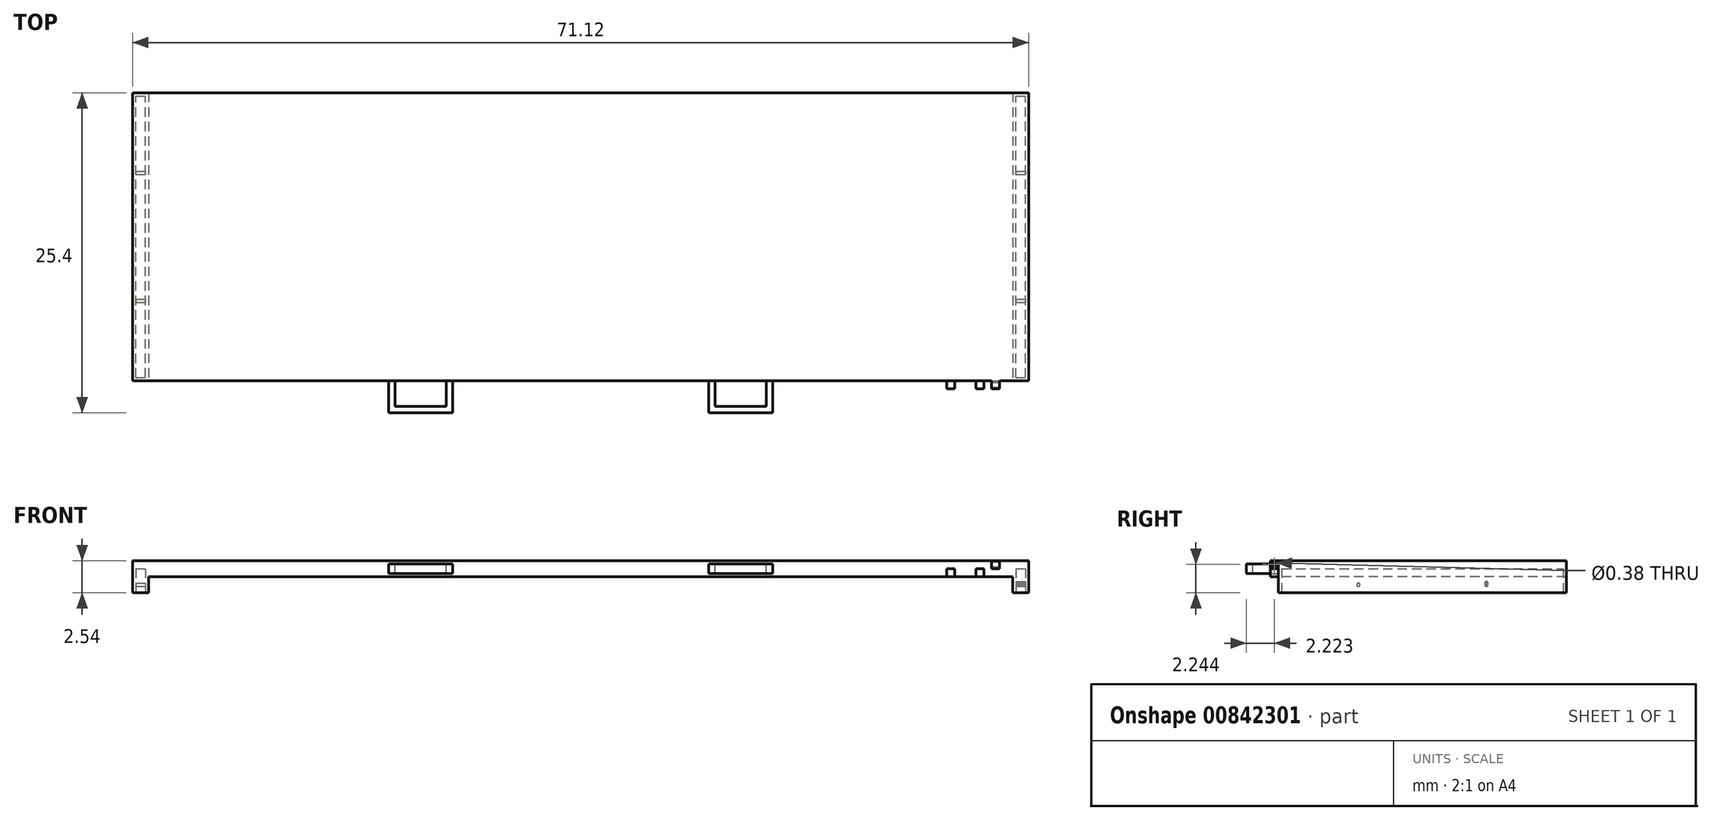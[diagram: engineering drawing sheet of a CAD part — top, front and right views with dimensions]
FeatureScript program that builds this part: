
annotation { "Feature Type Name" : "Feature", "Feature Type Description" : "" }
export const myFeature = defineFeature(function(context is Context, id is Id, definition is map)
    precondition{}
    {
        {
            var Q0;
            Q0=qCreatedBy(makeId("Front.planeOp"),FACE);
            var sketch = newSketch(context, id + "F0", { "sketchPlane" : qUnion([Q0])});
            skLineSegment(sketch, "E0.bottom", {"start": v(-23.07, 23.36) * mm, "end": v(48.05, 23.36) * mm});
            skLineSegment(sketch, "E0.top", {"start": v(-23.07, 20.82) * mm, "end": v(48.05, 20.82) * mm});
            skLineSegment(sketch, "E0.left", {"start": v(-23.07, 23.36) * mm, "end": v(-23.07, 20.82) * mm});
            skLineSegment(sketch, "E0.right", {"start": v(48.05, 23.36) * mm, "end": v(48.05, 20.82) * mm});
            skSolve(sketch);
        }
        {
            var Q0;
            Q0 = qSketchRegion(id + "F0", true);
            extrude(context, id + "F1", {"entities" : qUnion([Q0]), "depth" : 22.86 * mm, "offsetDistance" : 25.4 * mm});
        }
        {
            var Q0;
            Q0=makeQuery(id+"F1.opExtrude","CAP_FACE",FACE,{"disambiguationData":[OSD([sQuery(id+"F0.wireOp",EDGE,"E0.bottom"),sQuery(id+"F0.wireOp",EDGE,"E0.top"),sQuery(id+"F0.wireOp",EDGE,"E0.left"),sQuery(id+"F0.wireOp",EDGE,"E0.right")])],"isStart":false});
            var sketch = newSketch(context, id + "F2", { "sketchPlane" : qUnion([Q0])});
            skLineSegment(sketch, "E1.bottom", {"start": v(-21.8, 20.82) * mm, "end": v(46.78, 20.82) * mm});
            skLineSegment(sketch, "E1.top", {"start": v(-21.8, 22.1) * mm, "end": v(46.78, 22.1) * mm});
            skLineSegment(sketch, "E1.left", {"start": v(-21.8, 20.82) * mm, "end": v(-21.8, 22.1) * mm});
            skLineSegment(sketch, "E1.right", {"start": v(46.78, 20.82) * mm, "end": v(46.78, 22.1) * mm});
            skSolve(sketch);
        }
        {
            var Q0;
            Q0 = qSketchRegion(id + "F2", true);
            extrude(context, id + "F3", {"entities" : qUnion([Q0]), "operationType" : NewBodyOperationType.REMOVE, "oppositeDirection" : true, "depth" : 22.86 * mm, "offsetDistance" : 25.4 * mm});
        }
        {
            var Q0;
            {var subQ0=sQuery(id+"F0.wireOp",EDGE,"E0.right");var subQ2=sQuery(id+"F0.wireOp",EDGE,"E0.top");Q0=makeQuery(id+"F3.boolean.opBoolean","SPLIT",FACE,{"disambiguationData":[TD([makeQuery(id+"F1.opExtrude","SWEPT_FACE",FACE,{"disambiguationData":[OSD([subQ0])]})])],"derivedFrom":makeQuery(id+"F1.opExtrude","SWEPT_FACE",FACE,{"disambiguationData":[OSD([subQ2])]})});}
            var sketch = newSketch(context, id + "F4", { "sketchPlane" : qUnion([Q0])});
            skLineSegment(sketch, "E2.bottom", {"start": v(47.03, 22.6) * mm, "end": v(47.8, 22.6) * mm});
            skLineSegment(sketch, "E2.top", {"start": v(47.03, 0.25) * mm, "end": v(47.8, 0.25) * mm});
            skLineSegment(sketch, "E2.left", {"start": v(47.03, 22.6) * mm, "end": v(47.03, 0.25) * mm});
            skLineSegment(sketch, "E2.right", {"start": v(47.8, 22.6) * mm, "end": v(47.8, 0.25) * mm});
            skSolve(sketch);
        }
        {
            var Q0;
            Q0 = qSketchRegion(id + "F4", true);
            extrude(context, id + "F5", {"entities" : qUnion([Q0]), "operationType" : NewBodyOperationType.REMOVE, "oppositeDirection" : true, "depth" : 1.9 * mm, "offsetDistance" : 25.4 * mm});
        }
        {
            var Q0;
            {var subQ1=sQuery(id+"F0.wireOp",EDGE,"E0.left");var subQ2=sQuery(id+"F0.wireOp",EDGE,"E0.top");Q0=makeQuery(id+"F3.boolean.opBoolean","SPLIT",FACE,{"disambiguationData":[TD([makeQuery(id+"F1.opExtrude","SWEPT_FACE",FACE,{"disambiguationData":[OSD([subQ1])]})])],"derivedFrom":makeQuery(id+"F1.opExtrude","SWEPT_FACE",FACE,{"disambiguationData":[OSD([subQ2])]})});}
            var sketch = newSketch(context, id + "F6", { "sketchPlane" : qUnion([Q0])});
            skLineSegment(sketch, "E3.bottom", {"start": v(-22.82, 22.6) * mm, "end": v(-22.05, 22.6) * mm});
            skLineSegment(sketch, "E3.top", {"start": v(-22.82, 0.25) * mm, "end": v(-22.05, 0.25) * mm});
            skLineSegment(sketch, "E3.left", {"start": v(-22.82, 22.6) * mm, "end": v(-22.82, 0.25) * mm});
            skLineSegment(sketch, "E3.right", {"start": v(-22.05, 22.6) * mm, "end": v(-22.05, 0.25) * mm});
            skSolve(sketch);
        }
        {
            var Q0;
            Q0 = qSketchRegion(id + "F6", true);
            extrude(context, id + "F7", {"entities" : qUnion([Q0]), "operationType" : NewBodyOperationType.REMOVE, "oppositeDirection" : true, "depth" : 1.9 * mm, "offsetDistance" : 25.4 * mm});
        }
        {
            var Q0;
            Q0=makeQuery(id+"F5.boolean.opBoolean","COPY",FACE,{"derivedFrom":makeQuery(id+"F5.opExtrude","SWEPT_FACE",FACE,{"disambiguationData":[OSD([sQuery(id+"F4.wireOp",EDGE,"E2.right")])]})});
            var sketch = newSketch(context, id + "F8", { "sketchPlane" : qUnion([Q0])});
            skCircle(sketch, "E4", {"center": v(16.5, 21.46) * mm, "radius": 0.13 * mm});
            skCircle(sketch, "E5", {"center": v(6.35, 21.59) * mm, "radius": 0.13 * mm});
            skSolve(sketch);
        }
        {
            var Q0;
            Q0 = qSketchRegion(id + "F8", true);
            extrude(context, id + "F9", {"entities" : qUnion([Q0]), "operationType" : NewBodyOperationType.ADD, "endBound" : BoundingType.UP_TO_NEXT, "depth" : 25.4 * mm, "offsetDistance" : 25.4 * mm});
        }
        {
            var Q0;
            Q0=makeQuery(id+"F7.boolean.opBoolean","COPY",FACE,{"derivedFrom":makeQuery(id+"F7.opExtrude","SWEPT_FACE",FACE,{"disambiguationData":[OSD([sQuery(id+"F6.wireOp",EDGE,"E3.right")])]})});
            var sketch = newSketch(context, id + "F10", { "sketchPlane" : qUnion([Q0])});
            skCircle(sketch, "E6", {"center": v(16.51, 21.46) * mm, "radius": 0.13 * mm});
            skCircle(sketch, "E7", {"center": v(6.35, 21.46) * mm, "radius": 0.13 * mm});
            skSolve(sketch);
        }
        {
            var Q0;
            Q0 = qSketchRegion(id + "F10", true);
            extrude(context, id + "F11", {"entities" : qUnion([Q0]), "operationType" : NewBodyOperationType.ADD, "endBound" : BoundingType.UP_TO_NEXT, "depth" : 25.4 * mm, "offsetDistance" : 25.4 * mm});
        }
        {
            var Q0;
            Q0=makeQuery(id+"F1.opExtrude","CAP_FACE",FACE,{"disambiguationData":[OSD([sQuery(id+"F0.wireOp",EDGE,"E0.bottom"),sQuery(id+"F0.wireOp",EDGE,"E0.top"),sQuery(id+"F0.wireOp",EDGE,"E0.left"),sQuery(id+"F0.wireOp",EDGE,"E0.right")])],"isStart":false});
            var sketch = newSketch(context, id + "F12", { "sketchPlane" : qUnion([Q0])});
            skLineSegment(sketch, "E8.bottom", {"start": v(-2.75, 23.11) * mm, "end": v(2.33, 23.11) * mm});
            skLineSegment(sketch, "E8.top", {"start": v(-2.75, 22.35) * mm, "end": v(2.33, 22.35) * mm});
            skLineSegment(sketch, "E8.left", {"start": v(-2.75, 23.11) * mm, "end": v(-2.75, 22.35) * mm});
            skLineSegment(sketch, "E8.right", {"start": v(2.33, 23.11) * mm, "end": v(2.33, 22.35) * mm});
            skLineSegment(sketch, "E9.bottom", {"start": v(22.65, 23.11) * mm, "end": v(27.73, 23.11) * mm});
            skLineSegment(sketch, "E9.top", {"start": v(22.65, 22.35) * mm, "end": v(27.73, 22.35) * mm});
            skLineSegment(sketch, "E9.left", {"start": v(22.65, 23.11) * mm, "end": v(22.65, 22.35) * mm});
            skLineSegment(sketch, "E9.right", {"start": v(27.73, 23.11) * mm, "end": v(27.73, 22.35) * mm});
            skSolve(sketch);
        }
        {
            var Q0;
            Q0 = qSketchRegion(id + "F12", true);
            extrude(context, id + "F13", {"entities" : qUnion([Q0]), "operationType" : NewBodyOperationType.ADD, "depth" : 2.54 * mm, "offsetDistance" : 25.4 * mm});
        }
        {
            var Q0;
            Q0=makeQuery(id+"F13.opExtrude","SWEPT_FACE",FACE,{"disambiguationData":[OSD([sQuery(id+"F12.wireOp",EDGE,"E9.bottom")])]});
            var sketch = newSketch(context, id + "F14", { "sketchPlane" : qUnion([Q0])});
            skLineSegment(sketch, "E10.bottom", {"start": v(23.16, -22.86) * mm, "end": v(27.22, -22.86) * mm});
            skLineSegment(sketch, "E10.top", {"start": v(23.16, -24.9) * mm, "end": v(27.22, -24.9) * mm});
            skLineSegment(sketch, "E10.left", {"start": v(23.16, -22.86) * mm, "end": v(23.16, -24.9) * mm});
            skLineSegment(sketch, "E10.right", {"start": v(27.22, -22.86) * mm, "end": v(27.22, -24.9) * mm});
            skSolve(sketch);
        }
        {
            var Q0;
            Q0 = qSketchRegion(id + "F14", true);
            extrude(context, id + "F15", {"entities" : qUnion([Q0]), "operationType" : NewBodyOperationType.REMOVE, "endBound" : BoundingType.THROUGH_ALL, "oppositeDirection" : true, "depth" : 25.4 * mm, "offsetDistance" : 25.4 * mm});
        }
        {
            var Q0;
            Q0=makeQuery(id+"F13.opExtrude","SWEPT_FACE",FACE,{"disambiguationData":[OSD([sQuery(id+"F12.wireOp",EDGE,"E8.bottom")])]});
            var sketch = newSketch(context, id + "F16", { "sketchPlane" : qUnion([Q0])});
            skLineSegment(sketch, "E11.bottom", {"start": v(-2.24, -22.86) * mm, "end": v(1.82, -22.86) * mm});
            skLineSegment(sketch, "E11.top", {"start": v(-2.24, -24.9) * mm, "end": v(1.82, -24.9) * mm});
            skLineSegment(sketch, "E11.left", {"start": v(-2.24, -22.86) * mm, "end": v(-2.24, -24.9) * mm});
            skLineSegment(sketch, "E11.right", {"start": v(1.82, -22.86) * mm, "end": v(1.82, -24.9) * mm});
            skSolve(sketch);
        }
        {
            var Q0;
            Q0 = qSketchRegion(id + "F16", true);
            extrude(context, id + "F17", {"entities" : qUnion([Q0]), "operationType" : NewBodyOperationType.REMOVE, "endBound" : BoundingType.THROUGH_ALL, "oppositeDirection" : true, "depth" : 25.4 * mm, "offsetDistance" : 25.4 * mm});
        }
        {
            var Q0;
            Q0=makeQuery(id+"F17.boolean.opBoolean","MERGE",FACE,{"derivedFrom":[makeQuery(id+"F15.boolean.opBoolean","MERGE",FACE,{"derivedFrom":[makeQuery(id+"F1.opExtrude","CAP_FACE",FACE,{"disambiguationData":[OSD([sQuery(id+"F0.wireOp",EDGE,"E0.bottom"),sQuery(id+"F0.wireOp",EDGE,"E0.top"),sQuery(id+"F0.wireOp",EDGE,"E0.left"),sQuery(id+"F0.wireOp",EDGE,"E0.right")])],"isStart":false}),makeQuery(id+"F15.opExtrude","SWEPT_FACE",FACE,{"disambiguationData":[OSD([sQuery(id+"F14.wireOp",EDGE,"E10.bottom")])]})]}),makeQuery(id+"F17.opExtrude","SWEPT_FACE",FACE,{"disambiguationData":[OSD([sQuery(id+"F16.wireOp",EDGE,"E11.bottom")])]})]});
            var sketch = newSketch(context, id + "F18", { "sketchPlane" : qUnion([Q0])});
            skLineSegment(sketch, "E12.bottom", {"start": v(45.12, 23.36) * mm, "end": v(45.75, 23.36) * mm});
            skLineSegment(sketch, "E12.top", {"start": v(45.12, 22.73) * mm, "end": v(45.75, 22.73) * mm});
            skLineSegment(sketch, "E12.left", {"start": v(45.12, 23.36) * mm, "end": v(45.12, 22.73) * mm});
            skLineSegment(sketch, "E12.right", {"start": v(45.75, 23.36) * mm, "end": v(45.75, 22.73) * mm});
            skLineSegment(sketch, "E13.bottom", {"start": v(43.86, 22.1) * mm, "end": v(44.5, 22.1) * mm});
            skLineSegment(sketch, "E13.top", {"start": v(43.86, 22.73) * mm, "end": v(44.5, 22.73) * mm});
            skLineSegment(sketch, "E13.left", {"start": v(43.86, 22.1) * mm, "end": v(43.86, 22.73) * mm});
            skLineSegment(sketch, "E13.right", {"start": v(44.5, 22.1) * mm, "end": v(44.5, 22.73) * mm});
            skLineSegment(sketch, "E14.bottom", {"start": v(41.55, 22.1) * mm, "end": v(42.18, 22.1) * mm});
            skLineSegment(sketch, "E14.top", {"start": v(41.55, 22.73) * mm, "end": v(42.18, 22.73) * mm});
            skLineSegment(sketch, "E14.left", {"start": v(41.55, 22.1) * mm, "end": v(41.55, 22.73) * mm});
            skLineSegment(sketch, "E14.right", {"start": v(42.18, 22.1) * mm, "end": v(42.18, 22.73) * mm});
            skSolve(sketch);
        }
        {
            var Q0;
            Q0 = qSketchRegion(id + "F18", true);
            extrude(context, id + "F19", {"entities" : qUnion([Q0]), "operationType" : NewBodyOperationType.ADD, "depth" : 0.64 * mm, "offsetDistance" : 25.4 * mm});
        }
        {
            var Q0;
            Q0=makeQuery(id+"F19.opExtrude","SWEPT_FACE",FACE,{"disambiguationData":[OSD([sQuery(id+"F18.wireOp",EDGE,"E12.right")])]});
            var sketch = newSketch(context, id + "F20", { "sketchPlane" : qUnion([Q0])});
            skCircle(sketch, "E15", {"center": v(-23.18, 23.06) * mm, "radius": 0.2 * mm});
            skSolve(sketch);
        }
        {
            var Q0;
            Q0 = qSketchRegion(id + "F20", true);
            extrude(context, id + "F21", {"entities" : qUnion([Q0]), "operationType" : NewBodyOperationType.REMOVE, "oppositeDirection" : true, "depth" : 2.54 * mm, "offsetDistance" : 25.4 * mm});
        }
    });
